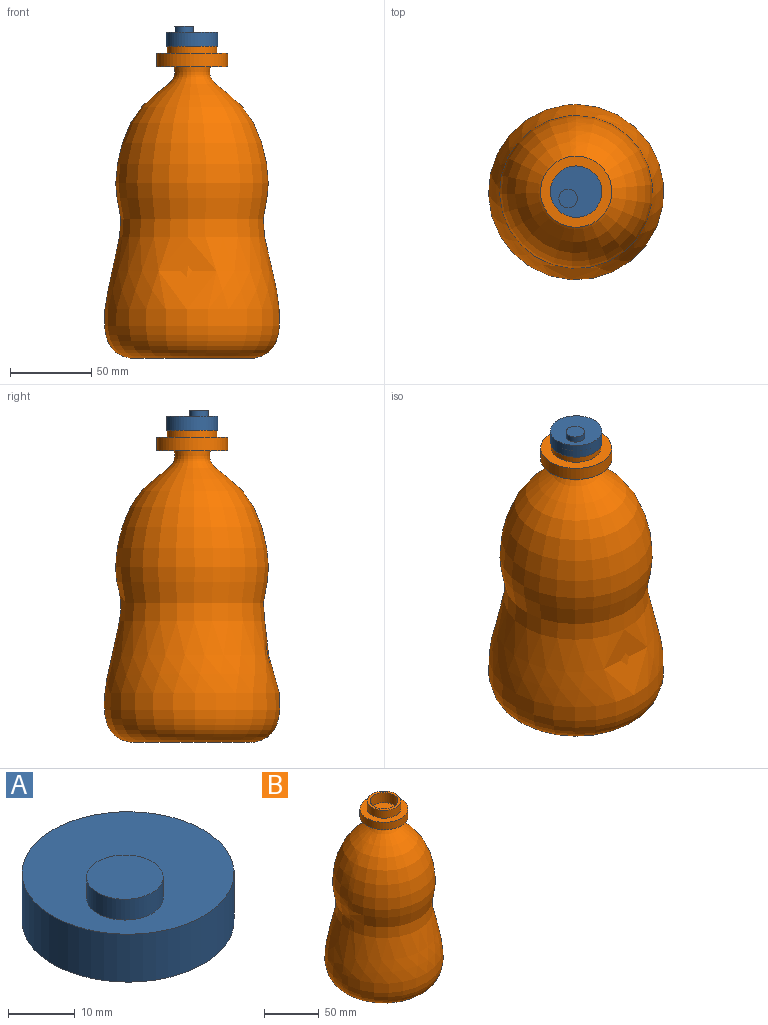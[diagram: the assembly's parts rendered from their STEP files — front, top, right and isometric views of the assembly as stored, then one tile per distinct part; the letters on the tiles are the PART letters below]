
ASSEMBLY  parts=2 mates=1
PART A: 7 faces, bbox 31.8x31.8x12.6 mm
  f0: cylinder r=15.88mm len=31.75mm, axis (0,0,-1), area 875.1mm2, adj f1,f2
  f1: plane 31.75x31.75mm, normal (0,0,1), area 688.3mm2, adj f0,f5
  f2: plane 31.75x31.75mm, normal (0,0,-1), area 105.2mm2, adj f0,f3
  f3: cylinder r=14.78mm len=29.57mm, axis (0,0,-1), area 713.5mm2, adj f2,f4
  f4: plane 29.57x29.57mm, normal (0,0,-1), area 686.5mm2, adj f3
  f5: cylinder r=5.74mm len=11.48mm, axis (0,0,-1), area 137.4mm2, adj f1,f6
  f6: plane 11.48x11.48mm, normal (0,0,1), area 103.5mm2, adj f5
PART B: 13 faces, bbox 108.4x108.4x196.9 mm
  f0: plane 30.65x30.65mm, normal (0,0,1), area 224.3mm2, adj f6,f12
  f1: plane 76.61x76.61mm, normal (0,0,-1), area 4609.9mm2, adj f2
  f2: revolved ~179.77x108.4mm, area 53039.9mm2, adj f1,f3
  f3: plane 43.92x43.92mm, normal (0,0,-1), area 1129mm2, adj f2,f4
  f4: cylinder r=21.96mm len=43.92mm, axis (0,0,-1), area 1145.8mm2, adj f3,f5
  f5: plane 43.92x43.92mm, normal (0,0,1), area 777.7mm2, adj f4,f6
  f6: cylinder r=15.32mm len=30.65mm, axis (0,0,-1), area 844.7mm2, adj f0,f5
  f7: plane 76.23x76.23mm, normal (0,0,1), area 4564.5mm2, adj f8
  f8: revolved ~179.77x103.28mm, area 48751.2mm2, adj f7,f9
  f9: plane 38.84x38.84mm, normal (0,0,1), area 939.3mm2, adj f8,f10
  f10: cylinder r=19.42mm len=38.84mm, axis (0,0,-1), area 393.3mm2, adj f9,f11
  f11: plane 38.84x38.84mm, normal (0,0,-1), area 671.7mm2, adj f10,f12
  f12: cylinder r=12.78mm len=25.57mm, axis (0,0,-1), area 908.7mm2, adj f0,f11
PLACE A t=(-11.93,4.32,206.2)mm
PLACE B rot(axis=(0,0,-1),90deg) t=(-11.93,4.32,117.13)mm
MATE cylindrical B.f4 <-> A.f0  axis (0,0,-1) through (-11.93,4.32,206.39)mm
